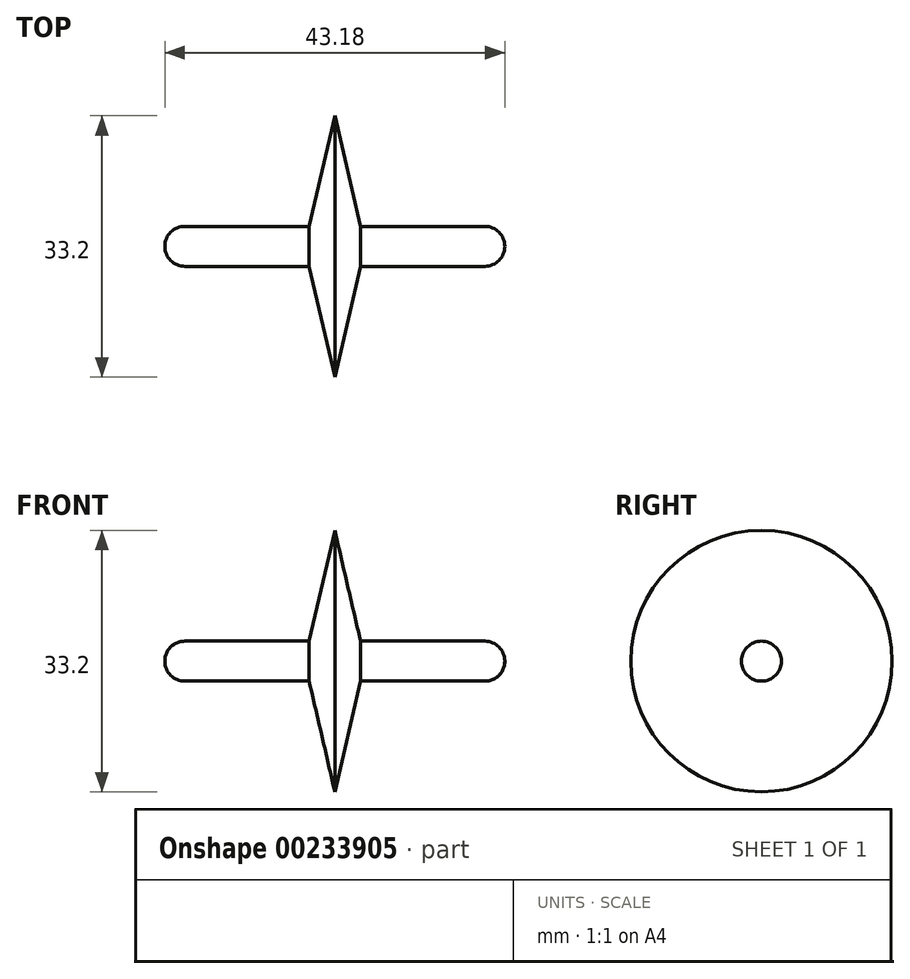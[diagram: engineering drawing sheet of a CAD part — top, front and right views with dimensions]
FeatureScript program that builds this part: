
annotation { "Feature Type Name" : "Feature", "Feature Type Description" : "" }
export const myFeature = defineFeature(function(context is Context, id is Id, definition is map)
    precondition{}
    {
        {
            var Q0;
            Q0=qCreatedBy(makeId("Front.planeOp"),FACE);
            var sketch = newSketch(context, id + "F0", { "sketchPlane" : qUnion([Q0])});
            skLineSegment(sketch, "E0", {"start": v(0, 16.6) * mm, "end": v(-3.85, 0) * mm});
            skLineSegment(sketch, "E1", {"start": v(0, 16.6) * mm, "end": v(3.85, 0) * mm});
            skLineSegment(sketch, "E2.bottom", {"start": v(19.05, -2.54) * mm, "end": v(-19.05, -2.54) * mm});
            skLineSegment(sketch, "E2.top", {"start": v(19.05, 2.54) * mm, "end": v(-19.05, 2.54) * mm});
            skLineSegment(sketch, "E2.left", {"start": v(19.05, -2.54) * mm, "end": v(19.05, 2.54) * mm});
            skLineSegment(sketch, "E2.right", {"start": v(-19.05, -2.54) * mm, "end": v(-19.05, 2.54) * mm});
            skPoint(sketch, "E2.middle", {"position": v(0, 0) * mm});
            skLineSegment(sketch, "E3", {"start": v(-19.05, 0) * mm, "end": v(26.55, 0) * mm});
            skArc(sketch, "E4", {"start": v(-19.05, 2.54) * mm, "mid": v(-21.59, 0) * mm, "end": v(-19.05, -2.54) * mm});
            skLineSegment(sketch, "E5", {"start": v(-19.05, 0) * mm, "end": v(-27.46, 0) * mm});
            skArc(sketch, "E6", {"start": v(19.05, -2.54) * mm, "mid": v(21.6, 0) * mm, "end": v(19.05, 2.54) * mm});
            skSolve(sketch);
        }
        {
            var Q0;
            {var subQ0=sQuery(id+"F0.wireOp",EDGE,"E1");var subQ1=sQuery(id+"F0.wireOp",EDGE,"E0");var subQ2=makeQuery(id+"F0.imprint","INTERSECT",VERTEX,{"derivedFrom":[subQ1,subQ0]});Q0=makeQuery(id+"F0.imprint","IMPRINT",FACE,{"disambiguationData":[TD([[makeQuery(id+"F0.imprint","IMPRINT",EDGE,{"disambiguationData":[TD([[subQ2,-1.0]])],"derivedFrom":subQ1}),1.0]])]});}
            var Q1;
            {var subQ0=sQuery(id+"F0.wireOp",EDGE,"E3");var subQ1=sQuery(id+"F0.wireOp",EDGE,"E0");var subQ2=makeQuery(id+"F0.imprint","INTERSECT",VERTEX,{"derivedFrom":[subQ1,subQ0]});Q1=makeQuery(id+"F0.imprint","IMPRINT",FACE,{"disambiguationData":[TD([[makeQuery(id+"F0.imprint","IMPRINT",EDGE,{"disambiguationData":[TD([[subQ2,1.0]])],"derivedFrom":subQ1}),1.0]])]});}
            var Q2;
            Q2=sQuery(id+"F0.wireOp",EDGE,"E3");
            revolve(context, id + "F1", {"entities" : qUnion([Q0, Q1]), "axis" : qUnion([Q2]), "revolveType" : RevolveType.FULL});
        }
        {
            var Q0;
            {var subQ0=sQuery(id+"F0.wireOp",EDGE,"E6");var subQ3=sQuery(id+"F0.wireOp",EDGE,"E3");var subQ5=makeQuery(id+"F0.imprint","INTERSECT",VERTEX,{"derivedFrom":[subQ3,subQ0]});Q0=makeQuery(id+"F0.imprint","IMPRINT",FACE,{"disambiguationData":[TD([[makeQuery(id+"F0.imprint","IMPRINT",EDGE,{"disambiguationData":[TD([[subQ5,1.0]])],"derivedFrom":subQ3}),1.0]])]});}
            var Q1;
            {var subQ0=sQuery(id+"F0.wireOp",EDGE,"E3");var subQ1=sQuery(id+"F0.wireOp",EDGE,"E1");var subQ2=makeQuery(id+"F0.imprint","INTERSECT",VERTEX,{"derivedFrom":[subQ1,subQ0]});Q1=makeQuery(id+"F0.imprint","IMPRINT",FACE,{"disambiguationData":[TD([[makeQuery(id+"F0.imprint","IMPRINT",EDGE,{"disambiguationData":[TD([[subQ2,1.0]])],"derivedFrom":subQ1}),1.0]])]});}
            var Q2;
            {var subQ0=sQuery(id+"F0.wireOp",EDGE,"E3");var subQ1=sQuery(id+"F0.wireOp",EDGE,"E0");var subQ2=makeQuery(id+"F0.imprint","INTERSECT",VERTEX,{"derivedFrom":[subQ1,subQ0]});Q2=makeQuery(id+"F0.imprint","IMPRINT",FACE,{"disambiguationData":[TD([[makeQuery(id+"F0.imprint","IMPRINT",EDGE,{"disambiguationData":[TD([[subQ2,1.0]])],"derivedFrom":subQ1}),1.0]])]});}
            var Q3;
            {var subQ0=sQuery(id+"F0.wireOp",EDGE,"E3");var subQ1=sQuery(id+"F0.wireOp",EDGE,"E0");var subQ2=makeQuery(id+"F0.imprint","INTERSECT",VERTEX,{"derivedFrom":[subQ1,subQ0]});Q3=makeQuery(id+"F0.imprint","IMPRINT",FACE,{"disambiguationData":[TD([[makeQuery(id+"F0.imprint","IMPRINT",EDGE,{"disambiguationData":[TD([[subQ2,1.0]])],"derivedFrom":subQ1}),-1.0]])]});}
            var Q4;
            {var subQ0=sQuery(id+"F0.wireOp",EDGE,"E4");var subQ3=sQuery(id+"F0.wireOp",EDGE,"E5");var subQ5=makeQuery(id+"F0.imprint","INTERSECT",VERTEX,{"derivedFrom":[subQ0,subQ3]});Q4=makeQuery(id+"F0.imprint","IMPRINT",FACE,{"disambiguationData":[TD([[makeQuery(id+"F0.imprint","IMPRINT",EDGE,{"disambiguationData":[TD([[subQ5,1.0]])],"derivedFrom":subQ0}),1.0]])]});}
            var Q5;
            Q5=sQuery(id+"F0.wireOp",EDGE,"E3");
            revolve(context, id + "F3", {"entities" : qUnion([Q0, Q1, Q2, Q3, Q4]), "axis" : qUnion([Q5]), "revolveType" : RevolveType.FULL});
        }
        {
            var Q0;
            {var subQ0=sQuery(id+"F0.wireOp",EDGE,"E1");var subQ1=sQuery(id+"F0.wireOp",EDGE,"E0");var subQ2=makeQuery(id+"F0.imprint","INTERSECT",VERTEX,{"derivedFrom":[subQ1,subQ0]});Q0=makeQuery(id+"F0.imprint","IMPRINT",FACE,{"disambiguationData":[TD([[makeQuery(id+"F0.imprint","IMPRINT",EDGE,{"disambiguationData":[TD([[subQ2,-1.0]])],"derivedFrom":subQ1}),1.0]])]});}
            var Q1;
            Q1=sQuery(id+"F0.wireOp",EDGE,"E3");
            revolve(context, id + "F2", {"operationType" : NewBodyOperationType.ADD, "entities" : qUnion([Q0]), "axis" : qUnion([Q1]), "revolveType" : RevolveType.FULL});
        }
    });
